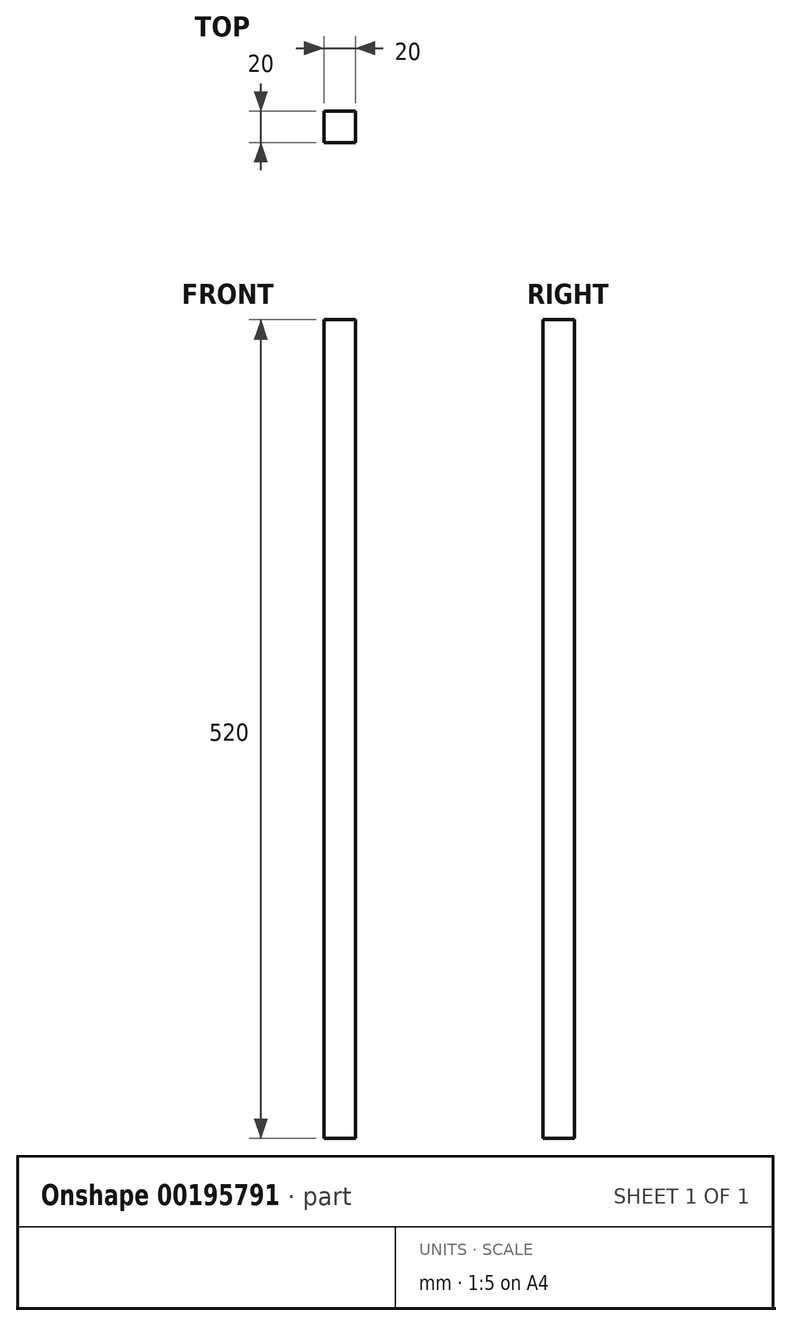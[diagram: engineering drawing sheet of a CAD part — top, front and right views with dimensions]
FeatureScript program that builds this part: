
annotation { "Feature Type Name" : "Feature", "Feature Type Description" : "" }
export const myFeature = defineFeature(function(context is Context, id is Id, definition is map)
    precondition{}
    {
        {
            var Q0;
            Q0=qCreatedBy(makeId("Top.planeOp"),FACE);
            var sketch = newSketch(context, id + "F0", { "sketchPlane" : qUnion([Q0])});
            skLineSegment(sketch, "E0.bottom", {"start": v(-114.13, -38.7) * mm, "end": v(-94.13, -38.7) * mm});
            skLineSegment(sketch, "E0.top", {"start": v(-114.13, -18.7) * mm, "end": v(-94.13, -18.7) * mm});
            skLineSegment(sketch, "E0.left", {"start": v(-114.13, -38.7) * mm, "end": v(-114.13, -18.7) * mm});
            skLineSegment(sketch, "E0.right", {"start": v(-94.13, -38.7) * mm, "end": v(-94.13, -18.7) * mm});
            skSolve(sketch);
        }
        {
            var Q0;
            Q0=makeQuery(id+"F0.imprint","IMPRINT",FACE,{"disambiguationData":[TD([[makeQuery(id+"F0.imprint","IMPRINT",EDGE,{"derivedFrom":sQuery(id+"F0.wireOp",EDGE,"E0.bottom")}),1.0]])]});
            extrude(context, id + "F1", {"entities" : qUnion([Q0]), "depth" : 520 * mm});
        }
    });
